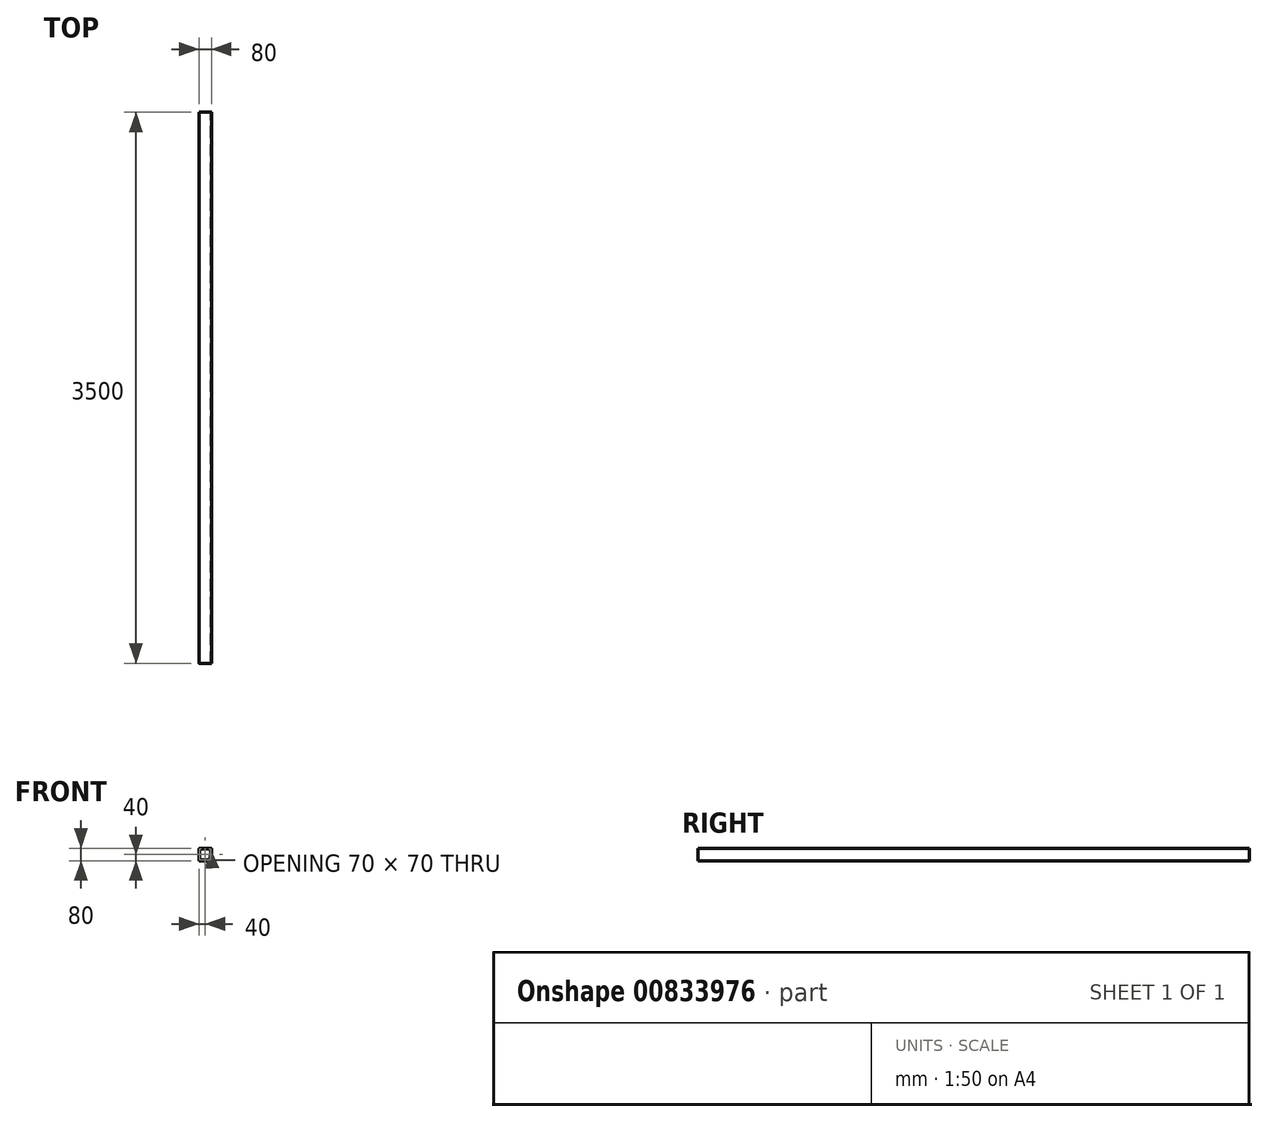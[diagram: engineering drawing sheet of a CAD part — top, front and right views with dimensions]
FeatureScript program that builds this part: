
annotation { "Feature Type Name" : "Feature", "Feature Type Description" : "" }
export const myFeature = defineFeature(function(context is Context, id is Id, definition is map)
    precondition{}
    {
        {
            var Q0;
            Q0=qCreatedBy(makeId("Front.planeOp"),FACE);
            var sketch = newSketch(context, id + "F0", { "sketchPlane" : qUnion([Q0])});
            skLineSegment(sketch, "E0.bottom", {"start": v(40, 40) * mm, "end": v(-40, 40) * mm});
            skLineSegment(sketch, "E0.top", {"start": v(40, -40) * mm, "end": v(-40, -40) * mm});
            skLineSegment(sketch, "E0.left", {"start": v(40, 40) * mm, "end": v(40, -40) * mm});
            skLineSegment(sketch, "E0.right", {"start": v(-40, 40) * mm, "end": v(-40, -40) * mm});
            skPoint(sketch, "E0.middle", {"position": v(0, 0) * mm});
            skLineSegment(sketch, "E1.bottom", {"start": v(35, 35) * mm, "end": v(-35, 35) * mm});
            skLineSegment(sketch, "E1.top", {"start": v(35, -35) * mm, "end": v(-35, -35) * mm});
            skLineSegment(sketch, "E1.left", {"start": v(35, 35) * mm, "end": v(35, -35) * mm});
            skLineSegment(sketch, "E1.right", {"start": v(-35, 35) * mm, "end": v(-35, -35) * mm});
            skSolve(sketch);
        }
        {
            var Q0;
            Q0=makeQuery(id+"F0.imprint","IMPRINT",FACE,{"disambiguationData":[TD([[makeQuery(id+"F0.imprint","IMPRINT",EDGE,{"derivedFrom":sQuery(id+"F0.wireOp",EDGE,"E0.bottom")}),1.0]])]});
            extrude(context, id + "F1", {"entities" : qUnion([Q0]), "depth" : 3500 * mm, "offsetDistance" : 25 * mm});
        }
        {
            var Q0;
            Q0=makeQuery(id+"F1.opExtrude","SWEPT_EDGE",EDGE,{"disambiguationData":[OSD([sQuery(id+"F0.wireOp",EDGE,"E1.top"),sQuery(id+"F0.wireOp",EDGE,"E1.left")])]});
            var Q1;
            Q1=makeQuery(id+"F1.opExtrude","SWEPT_EDGE",EDGE,{"disambiguationData":[OSD([sQuery(id+"F0.wireOp",EDGE,"E1.top"),sQuery(id+"F0.wireOp",EDGE,"E1.right")])]});
            var Q2;
            Q2=makeQuery(id+"F1.opExtrude","SWEPT_EDGE",EDGE,{"disambiguationData":[OSD([sQuery(id+"F0.wireOp",EDGE,"E1.bottom"),sQuery(id+"F0.wireOp",EDGE,"E1.left")])]});
            var Q3;
            Q3=makeQuery(id+"F1.opExtrude","SWEPT_EDGE",EDGE,{"disambiguationData":[OSD([sQuery(id+"F0.wireOp",EDGE,"E1.bottom"),sQuery(id+"F0.wireOp",EDGE,"E1.right")])]});
            fillet(context, id + "F2", {"entities" : qUnion([Q0, Q1, Q2, Q3]), "radius" : 3 * mm, "tangentPropagation" : true, "allowEdgeOverflow" : false});
        }
        {
            var Q0;
            Q0=makeQuery(id+"F1.opExtrude","SWEPT_EDGE",EDGE,{"disambiguationData":[OSD([sQuery(id+"F0.wireOp",EDGE,"E0.bottom"),sQuery(id+"F0.wireOp",EDGE,"E0.left")])]});
            var Q1;
            Q1=makeQuery(id+"F1.opExtrude","SWEPT_EDGE",EDGE,{"disambiguationData":[OSD([sQuery(id+"F0.wireOp",EDGE,"E0.bottom"),sQuery(id+"F0.wireOp",EDGE,"E0.right")])]});
            var Q2;
            Q2=makeQuery(id+"F1.opExtrude","SWEPT_EDGE",EDGE,{"disambiguationData":[OSD([sQuery(id+"F0.wireOp",EDGE,"E0.top"),sQuery(id+"F0.wireOp",EDGE,"E0.right")])]});
            var Q3;
            Q3=makeQuery(id+"F1.opExtrude","SWEPT_EDGE",EDGE,{"disambiguationData":[OSD([sQuery(id+"F0.wireOp",EDGE,"E0.top"),sQuery(id+"F0.wireOp",EDGE,"E0.left")])]});
            fillet(context, id + "F3", {"entities" : qUnion([Q0, Q1, Q2, Q3]), "radius" : 5 * mm, "tangentPropagation" : true, "allowEdgeOverflow" : false});
        }
    });
